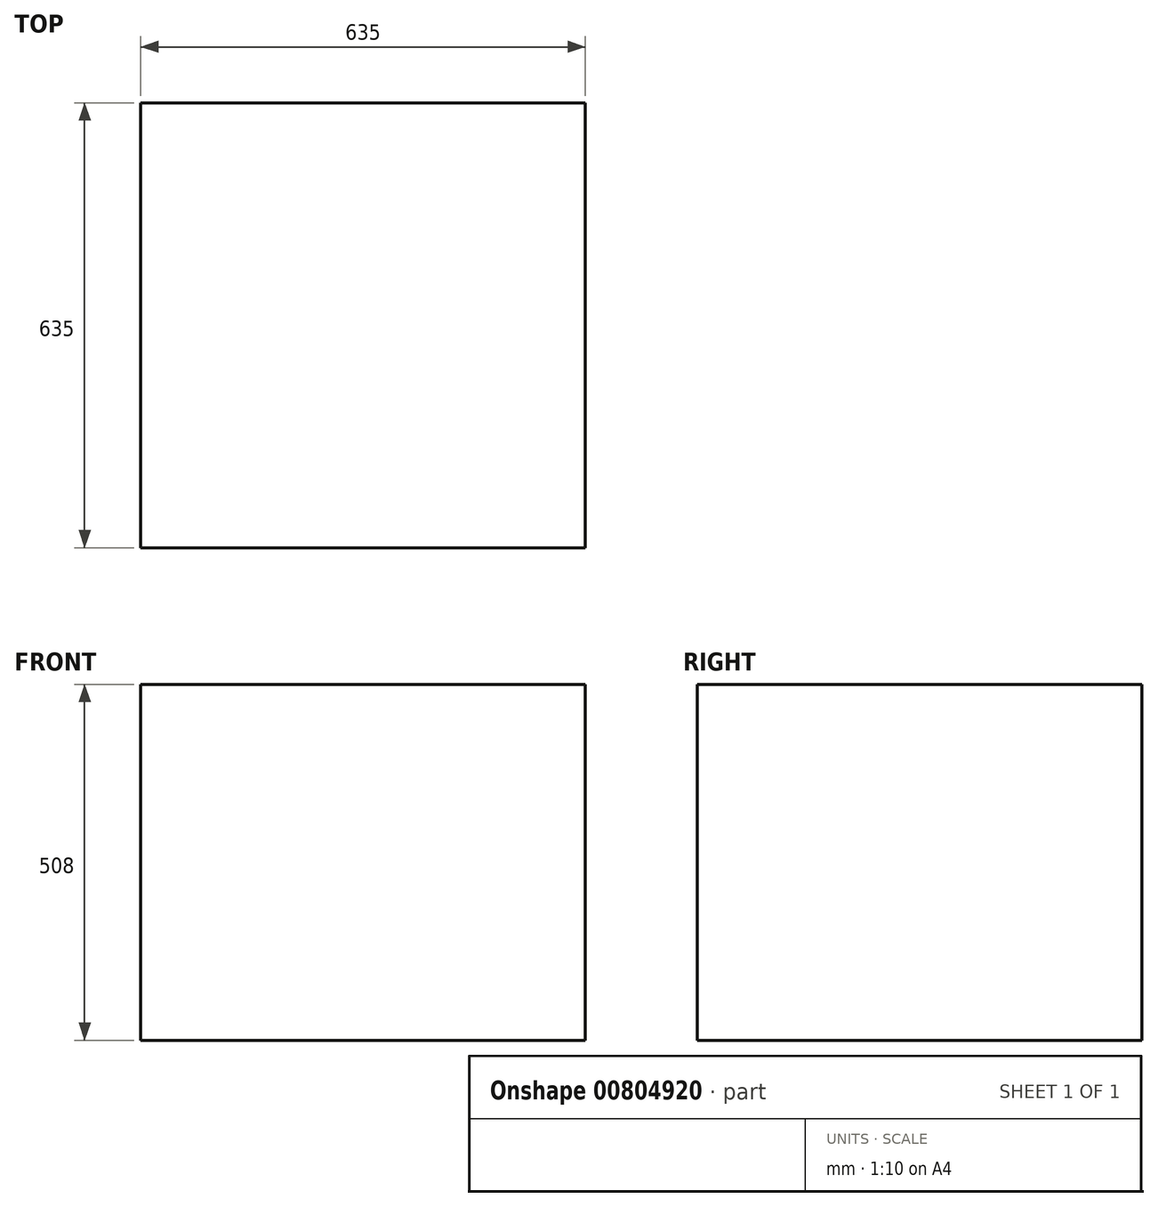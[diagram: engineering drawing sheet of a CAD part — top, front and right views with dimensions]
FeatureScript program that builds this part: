
annotation { "Feature Type Name" : "Feature", "Feature Type Description" : "" }
export const myFeature = defineFeature(function(context is Context, id is Id, definition is map)
    precondition{}
    {
        {
            var Q0;
            Q0=qCreatedBy(makeId("Top.planeOp"),FACE);
            var sketch = newSketch(context, id + "F0", { "sketchPlane" : qUnion([Q0])});
            skLineSegment(sketch, "E0.bottom", {"start": v(317.5, 317.5) * mm, "end": v(-317.5, 317.5) * mm});
            skLineSegment(sketch, "E0.top", {"start": v(317.5, -317.5) * mm, "end": v(-317.5, -317.5) * mm});
            skLineSegment(sketch, "E0.left", {"start": v(317.5, 317.5) * mm, "end": v(317.5, -317.5) * mm});
            skLineSegment(sketch, "E0.right", {"start": v(-317.5, 317.5) * mm, "end": v(-317.5, -317.5) * mm});
            skPoint(sketch, "E0.middle", {"position": v(0, 0) * mm});
            skSolve(sketch);
        }
        {
            var Q0;
            Q0=makeQuery(id+"F0.imprint","IMPRINT",FACE,{"disambiguationData":[TD([[makeQuery(id+"F0.imprint","IMPRINT",EDGE,{"derivedFrom":sQuery(id+"F0.wireOp",EDGE,"E0.bottom")}),1.0]])]});
            extrude(context, id + "F1", {"entities" : qUnion([Q0]), "depth" : 508 * mm, "offsetDistance" : 25.4 * mm});
        }
    });
